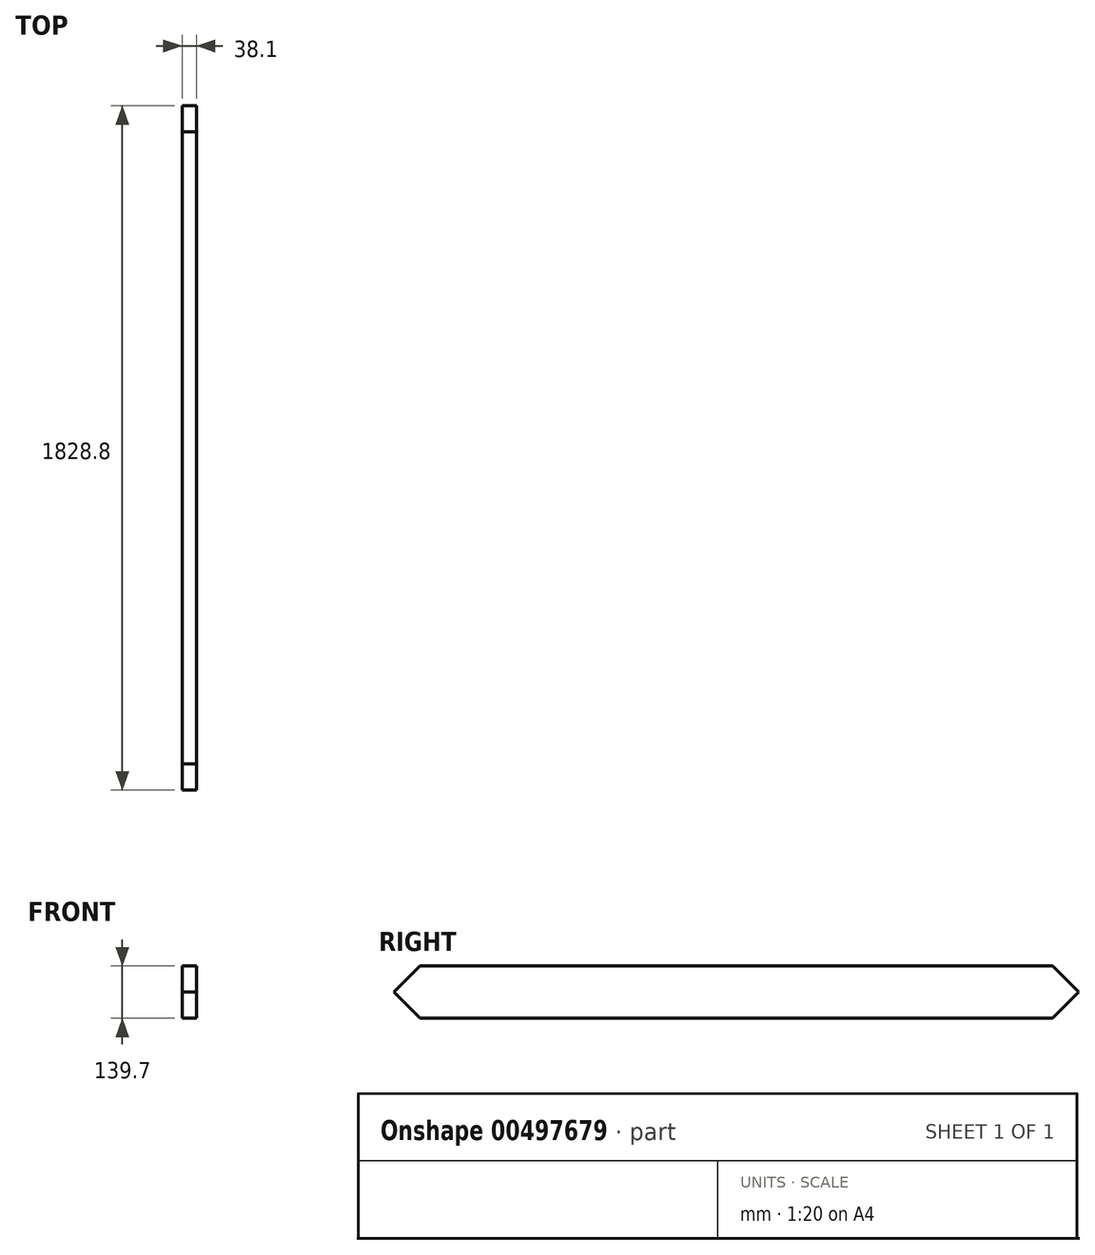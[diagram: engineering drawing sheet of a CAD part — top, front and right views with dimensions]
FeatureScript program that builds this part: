
annotation { "Feature Type Name" : "Feature", "Feature Type Description" : "" }
export const myFeature = defineFeature(function(context is Context, id is Id, definition is map)
    precondition{}
    {
        {
            var Q0;
            Q0=qCreatedBy(makeId("Front.planeOp"),FACE);
            var sketch = newSketch(context, id + "F0", { "sketchPlane" : qUnion([Q0])});
            skLineSegment(sketch, "E0.bottom", {"start": v(0, 0) * mm, "end": v(38.1, 0) * mm});
            skLineSegment(sketch, "E0.top", {"start": v(0, 139.7) * mm, "end": v(38.1, 139.7) * mm});
            skLineSegment(sketch, "E0.left", {"start": v(0, 0) * mm, "end": v(0, 139.7) * mm});
            skLineSegment(sketch, "E0.right", {"start": v(38.1, 0) * mm, "end": v(38.1, 139.7) * mm});
            skSolve(sketch);
        }
        {
            var Q0;
            Q0 = qSketchRegion(id + "F0", true);
            extrude(context, id + "F1", {"entities" : qUnion([Q0]), "depth" : 1828.8 * mm});
        }
        {
            var Q0;
            Q0=makeQuery(id+"F1.opExtrude","SWEPT_FACE",FACE,{"disambiguationData":[OSD([sQuery(id+"F0.wireOp",EDGE,"E0.right")])]});
            var sketch = newSketch(context, id + "F2", { "sketchPlane" : qUnion([Q0])});
            skLineSegment(sketch, "E1", {"start": v(-1828.8, 69.85) * mm, "end": v(-1758.95, 0) * mm});
            skLineSegment(sketch, "E2", {"start": v(-1758.95, 0) * mm, "end": v(-1828.8, 0) * mm});
            skLineSegment(sketch, "E3", {"start": v(-1828.8, 0) * mm, "end": v(-1828.8, 69.85) * mm});
            skLineSegment(sketch, "E4", {"start": v(-1828.8, 69.85) * mm, "end": v(-1758.95, 139.7) * mm});
            skLineSegment(sketch, "E5", {"start": v(-1758.95, 139.7) * mm, "end": v(-1828.8, 139.7) * mm});
            skLineSegment(sketch, "E6", {"start": v(-1828.8, 139.7) * mm, "end": v(-1828.8, 69.85) * mm});
            skLineSegment(sketch, "E7", {"start": v(0, 139.7) * mm, "end": v(0, 69.85) * mm});
            skLineSegment(sketch, "E8", {"start": v(0, 69.85) * mm, "end": v(-69.85, 139.7) * mm});
            skLineSegment(sketch, "E9", {"start": v(-69.85, 139.7) * mm, "end": v(0, 139.7) * mm});
            skLineSegment(sketch, "E10", {"start": v(0, 69.85) * mm, "end": v(0, 0) * mm});
            skLineSegment(sketch, "E11", {"start": v(0, 0) * mm, "end": v(-69.85, 0) * mm});
            skLineSegment(sketch, "E12", {"start": v(-69.85, 0) * mm, "end": v(0, 69.85) * mm});
            skSolve(sketch);
        }
        {
            var Q0;
            Q0 = qSketchRegion(id + "F2", true);
            extrude(context, id + "F3", {"entities" : qUnion([Q0]), "operationType" : NewBodyOperationType.REMOVE, "endBound" : BoundingType.THROUGH_ALL, "oppositeDirection" : true, "depth" : 25.4 * mm});
        }
    });
